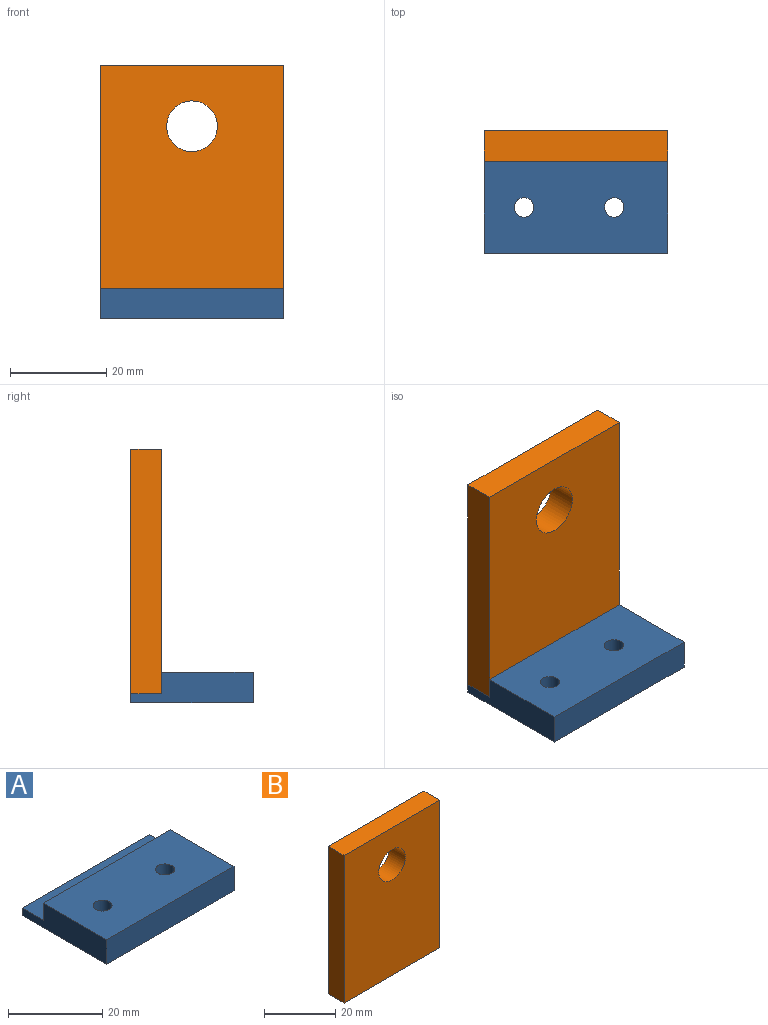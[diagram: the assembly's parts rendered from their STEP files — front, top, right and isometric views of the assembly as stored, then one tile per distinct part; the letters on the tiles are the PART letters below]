
ASSEMBLY  parts=2 mates=1
PART A: 10 faces, bbox 38.1x25.4x6.4 mm
  f0: plane 25.4x6.35mm, normal (1,0,0), area 133.1mm2, adj f1,f3,f4,f5,f6,f7
  f1: plane 38.1x1.91mm, normal (0,1,0), area 72.6mm2, adj f0,f2,f4,f6
  f2: plane 25.4x6.35mm, normal (-1,0,0), area 133.1mm2, adj f1,f3,f4,f5,f6,f7
  f3: plane 38.1x19.05mm, normal (0,0,1), area 700.2mm2, adj f0,f2,f5,f7,f8,f9
  f4: plane 38.1x25.4mm, normal (0,0,-1), area 942.1mm2, adj f0,f1,f2,f5,f8,f9
  f5: plane 38.1x6.35mm, normal (0,-1,0), area 241.9mm2, adj f0,f2,f3,f4
  f6: plane 38.1x6.35mm, normal (0,0,1), area 241.9mm2, adj f0,f1,f2,f7
  f7: plane 38.1x4.45mm, normal (0,1,0), area 169.4mm2, adj f0,f2,f3,f6
  f8: cylinder r=2.02mm len=6.35mm, axis (0,0,1), area 80.6mm2, adj f3,f4
  f9: cylinder r=2.02mm len=6.35mm, axis (0,0,1), area 80.6mm2, adj f3,f4
PART B: 7 faces, bbox 38.1x6.4x50.8 mm
  f0: plane 50.8x6.35mm, normal (-1,0,0), area 322.6mm2, adj f1,f3,f4,f5
  f1: plane 38.1x6.35mm, normal (0,0,-1), area 241.9mm2, adj f0,f2,f4,f5
  f2: plane 50.8x6.35mm, normal (1,0,0), area 322.6mm2, adj f1,f3,f4,f5
  f3: plane 38.1x6.35mm, normal (0,0,1), area 241.9mm2, adj f0,f2,f4,f5
  f4: plane 50.8x38.1mm, normal (0,-1,0), area 1848.2mm2, adj f0,f1,f2,f3,f6
  f5: plane 50.8x38.1mm, normal (0,1,0), area 1848.2mm2, adj f0,f1,f2,f3,f6
  f6: cylinder r=5.27mm len=10.54mm, axis (0,1,0), area 210.3mm2, adj f4,f5
PLACE A t=(1.83,-15.09,-3.09)mm
PLACE B t=(0.01,12.76,24.21)mm
MATE fastened B.f4 <-> A.f7  axis (0,-1,0) through (0.01,6.41,-1.19)mm
